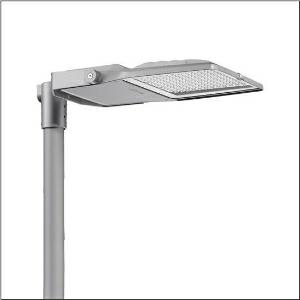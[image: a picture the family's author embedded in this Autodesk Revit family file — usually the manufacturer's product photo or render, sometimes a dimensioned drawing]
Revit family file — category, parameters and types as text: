
# Revit family: floodlight_fl_21_iq_midi___pl33t_5xa7781f2f3a_a5b2
name_source: partatom
category: Lighting Fixtures
units: mm (PartAtom-declared; Revit-internal decimal feet)

## family parameters
Cut with Voids When Loaded = No
Host = Face
Light Source = No
Part Type = Normal
Room Calculation Point = No
Round Connector Dimension = Use Diameter
Shared = No

## types (1)
- --- (1 x LED, 35350 lm, 270.2 W, 3000K)
    Apparent Load = 270 VA
    CIE Flux Codes = 26 75 99 100 100
    Color Rendering = 70
    Color Temperature = 3000K
    Default Elevation = 1800 mm
    Description = Floodlight FL 21 iQ midi, floodlight, primary light control with lens, of PMMA, primary optical cover: protective disc, of toughened safety glass, transparent, light distribution: PL33T, light emission: direct distribution, installation type: surface-mounted, lamps: LED, High Power LED, rated values: 35.350lm | 270,2W | 130,8lm/W (begin service life); end service life: 35.350lm | 286,6W; at 50% lumin. flux: 17.675lm | 117,4W | 150,6lm/W, colour temperature: 3000K, colour rendering: CRI > 70, light colour: 730, light setting 1 begin service life: 100% | 35.350lm | 270,2W | 130,8lm/W | 3.000K, light setting 1 end service life: 286,6W, further light settings possible, control: optimised constant luminous flux control (CLO 2.0), Desk-Remote (wireless, voltage-free reading and setting of iQ features in the workshop via application-optimized NFC function/RFID function), Light-Fading, Smart-Wire, Night-Set, Lumen-Switch, Temp-Guard, Auto-Match, pre-setting: linear dimming characteristic, with terminal, 6-pole, mains connection: 220..240V, AC, 50/60Hz, luminaire housing, of diecast aluminium, powder-coated, SITECO metallic grey (DB 702S), corrosivity category C5 mid according to DIN EN ISO 12944suitable for swimming poolschlorine-resistant, sealing non-destructively replaceable, please order mast flange separately, mast bracket, of steel, galvanised, powder-coated, SITECO metallic grey (DB 702S), protection rating (complete): IP66, insulation class (complete): insulation class II (safety insulation), certification: CE, ENEC, VDE, protection symbol: D, impact resistance: IK08, permissible operating ambient temperature: -40..+40°C, permissible operating ambient temperature for outdoor applications: -40..+50°C, standard: DIN EN 12944, LABS conformity tested according to VDMA 24364:2018-05, packaging unit: 1 piece

Light Distribution: PL33T
    Height = 76 mm
    Lamp = 1 x LED
    Lamp Light Flux = 35350 lm
    Lamp Power = 270.2 W
    Lamp count = 1
    Length = 657 mm
    Luminous efficacy = 131 lm/W
    Manufacturer = Siteco
    ModVariant = No
    Model = 5XA7781F2F3A
    Number of Poles = 1
    OnlyDefault = Yes
    Power Factor = 1
    Product Name = Floodlight FL 21 iQ midi | PL33T
    Product group = floodlight | pylon annexe
    ProductGroupID = 6201
    Protection Class = Protection class II
    Protection Degree = IP 66
    RLX_Detail_Level = 1
    RLX_Emergency_Light_Flux = 0 lm
    RLX_Emergency_Type = 0
    RLX_Emergency_Type_DB = No
    RlxData = <blob elided: 153765 chars, md5=7a5bd1f6>
    Socket = socket
    Standby Power = 0 W
    System Light Flux = 35350 lm
    System Power = 270 W
    Type Comments = factory setting: luminous flux: 100 % | dim-lin: 254 | 620 mA
    Type Image = l_1007123.jpg
    URL = http://relux.com
    VarID = @adj_103509
    Voltage = 0 V
    Weight = 0.00 kg
    Width = 442 mm

## geometry (parser evidence)
native form markers: Blend x4, Sweep x13
no freeform markers — native parametric forms only
